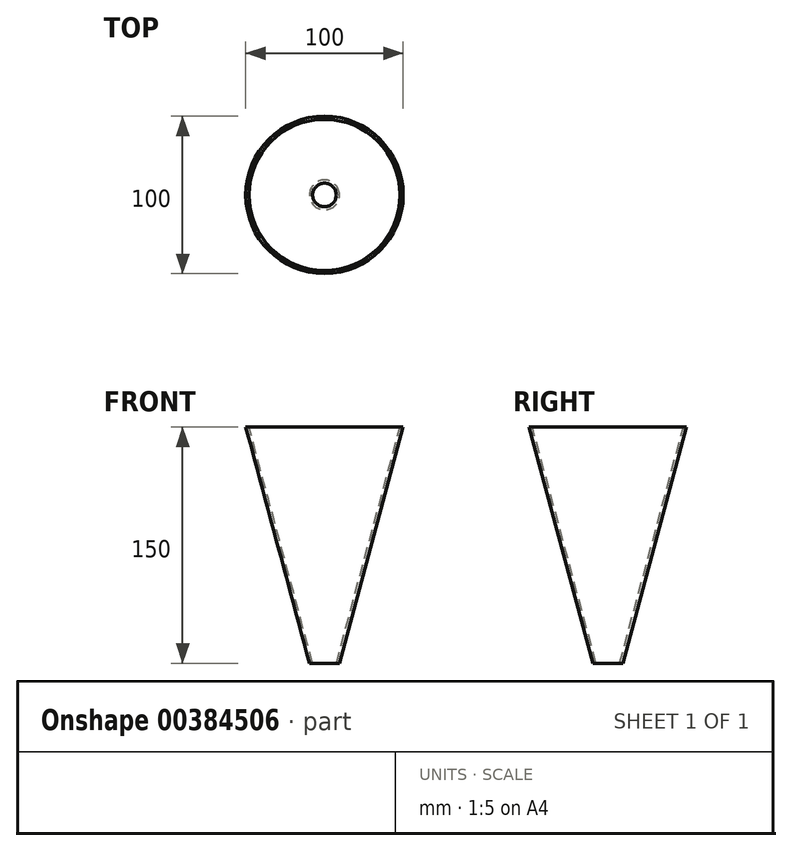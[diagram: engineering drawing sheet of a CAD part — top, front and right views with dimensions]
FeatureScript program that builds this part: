
annotation { "Feature Type Name" : "Feature", "Feature Type Description" : "" }
export const myFeature = defineFeature(function(context is Context, id is Id, definition is map)
    precondition{}
    {
        {
            var Q0;
            Q0=qCreatedBy(makeId("Front.planeOp"),FACE);
            var sketch = newSketch(context, id + "F0", { "sketchPlane" : qUnion([Q0])});
            skLineSegment(sketch, "E0", {"start": v(9.5, 0) * mm, "end": v(50, 150) * mm});
            skLineSegment(sketch, "E1", {"start": v(50, 150) * mm, "end": v(48, 150) * mm});
            skLineSegment(sketch, "E2", {"start": v(48, 150) * mm, "end": v(7.5, 0) * mm});
            skLineSegment(sketch, "E3", {"start": v(7.5, 0) * mm, "end": v(9.5, 0) * mm});
            skLineSegment(sketch, "E4", {"start": v(0, -15.65) * mm, "end": v(0, 118.21) * mm, "construction": true});
            skSolve(sketch);
        }
        {
            var Q0;
            Q0=makeQuery(id+"F0.imprint","IMPRINT",FACE,{"disambiguationData":[TD([[makeQuery(id+"F0.imprint","IMPRINT",EDGE,{"derivedFrom":sQuery(id+"F0.wireOp",EDGE,"E0")}),1.0]])]});
            var Q1;
            Q1=sQuery(id+"F0.wireOp",EDGE,"E4");
            revolve(context, id + "F1", {"entities" : qUnion([Q0]), "axis" : qUnion([Q1]), "revolveType" : RevolveType.FULL});
        }
    });
